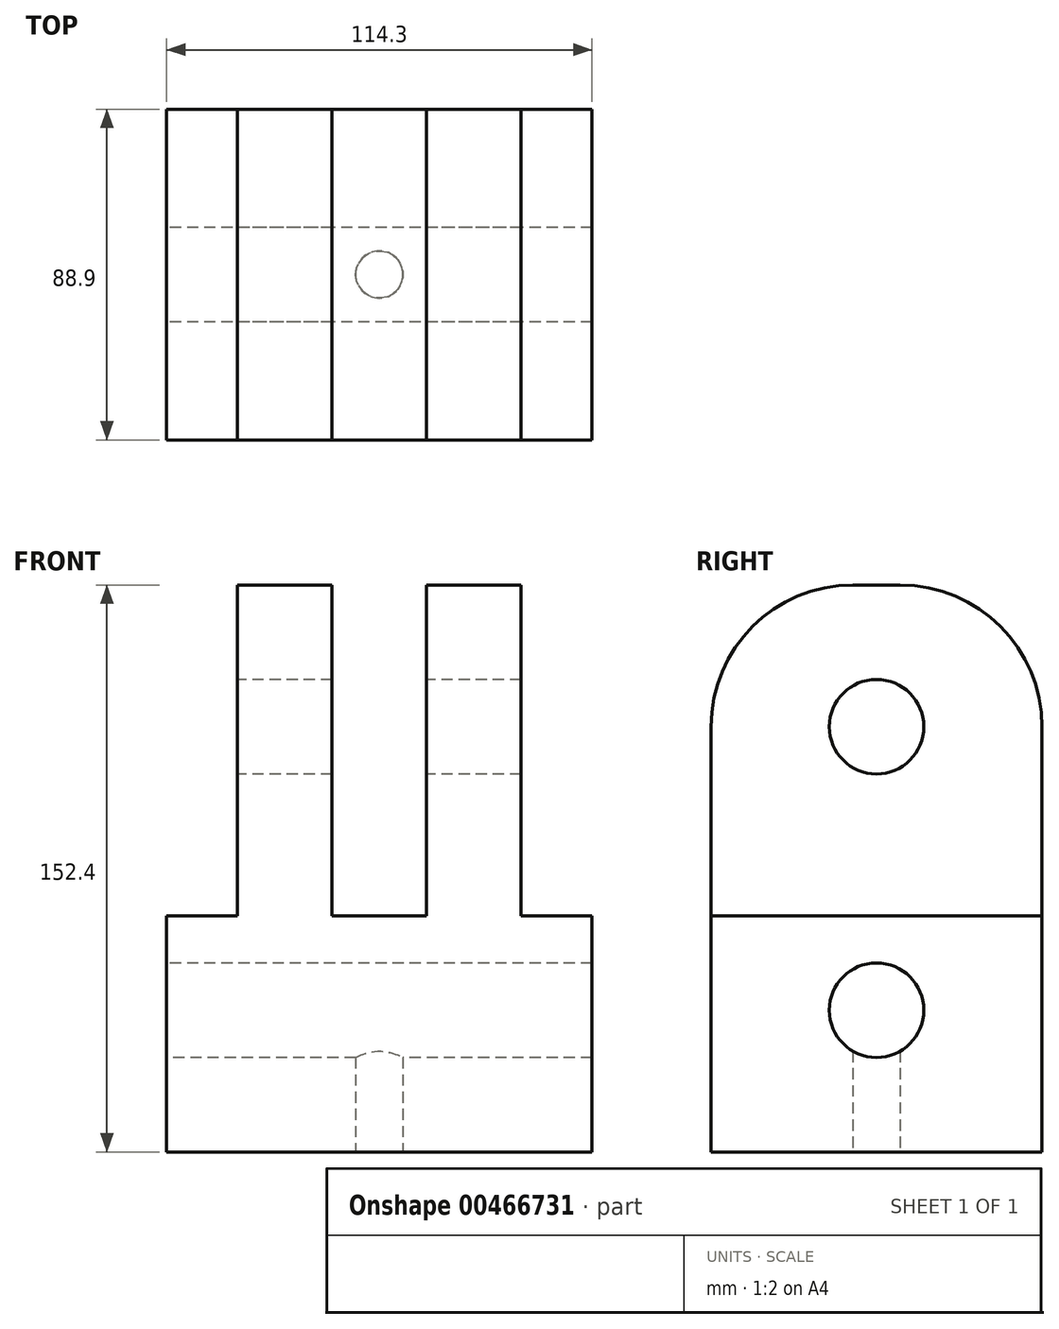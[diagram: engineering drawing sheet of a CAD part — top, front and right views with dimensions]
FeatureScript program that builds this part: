
annotation { "Feature Type Name" : "Feature", "Feature Type Description" : "" }
export const myFeature = defineFeature(function(context is Context, id is Id, definition is map)
    precondition{}
    {
        {
            var Q0;
            Q0=qCreatedBy(makeId("Top.planeOp"),FACE);
            var sketch = newSketch(context, id + "F0", { "sketchPlane" : qUnion([Q0])});
            skLineSegment(sketch, "E0.bottom", {"start": v(57.15, -44.45) * mm, "end": v(-57.15, -44.45) * mm});
            skLineSegment(sketch, "E0.top", {"start": v(57.15, 44.45) * mm, "end": v(-57.15, 44.45) * mm});
            skLineSegment(sketch, "E0.left", {"start": v(57.15, -44.45) * mm, "end": v(57.15, 44.45) * mm});
            skLineSegment(sketch, "E0.right", {"start": v(-57.15, -44.45) * mm, "end": v(-57.15, 44.45) * mm});
            skPoint(sketch, "E0.middle", {"position": v(0, 0) * mm});
            skSolve(sketch);
        }
        {
            var Q0;
            Q0=qSketchRegion(id+"F0",true);
            extrude(context, id + "F1", {"entities" : qUnion([Q0]), "depth" : 152.4 * mm});
        }
        {
            var Q0;
            Q0=makeQuery(id+"F1.opExtrude","SWEPT_FACE",FACE,{"disambiguationData":[OSD([sQuery(id+"F0.wireOp",EDGE,"E0.bottom")])]});
            var sketch = newSketch(context, id + "F2", { "sketchPlane" : qUnion([Q0])});
            skLineSegment(sketch, "E1.top", {"start": v(38.1, 63.5) * mm, "end": v(12.7, 63.5) * mm});
            skLineSegment(sketch, "E1.left", {"start": v(38.1, 152.4) * mm, "end": v(38.1, 63.5) * mm});
            skLineSegment(sketch, "E2.bottom", {"start": v(-12.7, 152.4) * mm, "end": v(-38.1, 152.4) * mm});
            skLineSegment(sketch, "E2.top", {"start": v(-12.7, 63.5) * mm, "end": v(-38.1, 63.5) * mm});
            skLineSegment(sketch, "E2.left", {"start": v(-12.7, 152.4) * mm, "end": v(-12.7, 63.5) * mm});
            skLineSegment(sketch, "E2.right", {"start": v(-38.1, 152.4) * mm, "end": v(-38.1, 63.5) * mm});
            skLineSegment(sketch, "E3", {"start": v(12.7, 152.4) * mm, "end": v(12.7, 63.5) * mm});
            skLineSegment(sketch, "E4", {"start": v(12.7, 63.5) * mm, "end": v(-12.7, 63.5) * mm});
            skLineSegment(sketch, "E5", {"start": v(-38.1, 63.5) * mm, "end": v(-57.15, 63.5) * mm});
            skPoint(sketch, "E5.endSnap0", {"position": v(-57.15, 76.2) * mm});
            skLineSegment(sketch, "E6", {"start": v(-57.15, 63.5) * mm, "end": v(38.1, 63.5) * mm});
            skLineSegment(sketch, "E7", {"start": v(38.1, 63.5) * mm, "end": v(57.15, 63.5) * mm});
            skSolve(sketch);
        }
        {
            var Q0;
            {var subQ0=sQuery(id+"F0.wireOp",EDGE,"E0.bottom");var subQ1=sQuery(id+"F0.wireOp",EDGE,"E0.left");Q0=makeQuery(id+"F6yg6DHshiw01AB_1.boolean.opBoolean","SPLIT",EDGE,{"disambiguationData":[TD([makeQuery(id+"F1.opExtrude","SWEPT_FACE",FACE,{"disambiguationData":[OSD([subQ1])]})])],"derivedFrom":makeQuery(id+"F1.opExtrude","CAP_EDGE",EDGE,{"disambiguationData":[OSD([subQ0])],"isStart":false})});}
            var Q1;
            {var subQ0=sQuery(id+"F0.wireOp",EDGE,"E0.bottom");Q1=makeQuery(id+"F6yg6DHshiw01AB_1.boolean.opBoolean","SPLIT",EDGE,{"disambiguationData":[TD([makeQuery(id+"F6yg6DHshiw01AB_1.opExtrude","SWEPT_FACE",FACE,{"disambiguationData":[OSD([sQuery(id+"F2.wireOp",EDGE,"E2.left")])]})])],"derivedFrom":makeQuery(id+"F1.opExtrude","CAP_EDGE",EDGE,{"disambiguationData":[OSD([subQ0])],"isStart":false})});}
            var Q2;
            {var subQ0=sQuery(id+"F0.wireOp",EDGE,"E0.bottom");var subQ1=sQuery(id+"F0.wireOp",EDGE,"E0.right");Q2=makeQuery(id+"F6yg6DHshiw01AB_1.boolean.opBoolean","SPLIT",EDGE,{"disambiguationData":[TD([makeQuery(id+"F1.opExtrude","SWEPT_FACE",FACE,{"disambiguationData":[OSD([subQ1])]})])],"derivedFrom":makeQuery(id+"F1.opExtrude","CAP_EDGE",EDGE,{"disambiguationData":[OSD([subQ0])],"isStart":false})});}
            var Q3;
            {var subQ0=sQuery(id+"F0.wireOp",EDGE,"E0.right");var subQ1=sQuery(id+"F0.wireOp",EDGE,"E0.top");Q3=makeQuery(id+"F6yg6DHshiw01AB_1.boolean.opBoolean","SPLIT",EDGE,{"disambiguationData":[TD([makeQuery(id+"F1.opExtrude","SWEPT_FACE",FACE,{"disambiguationData":[OSD([subQ0])]})])],"derivedFrom":makeQuery(id+"F1.opExtrude","CAP_EDGE",EDGE,{"disambiguationData":[OSD([subQ1])],"isStart":false})});}
            var Q4;
            {var subQ0=sQuery(id+"F0.wireOp",EDGE,"E0.top");Q4=makeQuery(id+"F6yg6DHshiw01AB_1.boolean.opBoolean","SPLIT",EDGE,{"disambiguationData":[TD([makeQuery(id+"F6yg6DHshiw01AB_1.opExtrude","SWEPT_FACE",FACE,{"disambiguationData":[OSD([sQuery(id+"F2.wireOp",EDGE,"E2.left")])]})])],"derivedFrom":makeQuery(id+"F1.opExtrude","CAP_EDGE",EDGE,{"disambiguationData":[OSD([subQ0])],"isStart":false})});}
            var Q5;
            {var subQ0=sQuery(id+"F0.wireOp",EDGE,"E0.left");var subQ1=sQuery(id+"F0.wireOp",EDGE,"E0.top");Q5=makeQuery(id+"F6yg6DHshiw01AB_1.boolean.opBoolean","SPLIT",EDGE,{"disambiguationData":[TD([makeQuery(id+"F1.opExtrude","SWEPT_FACE",FACE,{"disambiguationData":[OSD([subQ0])]})])],"derivedFrom":makeQuery(id+"F1.opExtrude","CAP_EDGE",EDGE,{"disambiguationData":[OSD([subQ1])],"isStart":false})});}
            fillet(context, id + "F3", {"entities" : qUnion([Q0, Q1, Q2, Q3, Q4, Q5]), "radius" : 38.1 * mm, "tangentPropagation" : true, "allowEdgeOverflow" : false});
        }
        {
            var Q0;
            Q0=makeQuery(id+"F1.opExtrude","SWEPT_FACE",FACE,{"disambiguationData":[OSD([sQuery(id+"F0.wireOp",EDGE,"E0.right")])]});
            var sketch = newSketch(context, id + "F4", { "sketchPlane" : qUnion([Q0])});
            skCircle(sketch, "E8", {"center": v(0, 38.1) * mm, "radius": 12.7 * mm});
            skCircle(sketch, "E9", {"center": v(0, 114.3) * mm, "radius": 12.7 * mm});
            skSolve(sketch);
        }
        {
            var Q0;
            Q0=qSketchRegion(id+"F4",true);
            extrude(context, id + "F5", {"entities" : qUnion([Q0]), "operationType" : NewBodyOperationType.REMOVE, "endBound" : BoundingType.THROUGH_ALL, "oppositeDirection" : true, "depth" : 25.4 * mm});
        }
        {
            var Q0;
            Q0=makeQuery(id+"F1.opExtrude","CAP_FACE",FACE,{"disambiguationData":[OSD([sQuery(id+"F0.wireOp",EDGE,"E0.bottom"),sQuery(id+"F0.wireOp",EDGE,"E0.top"),sQuery(id+"F0.wireOp",EDGE,"E0.left"),sQuery(id+"F0.wireOp",EDGE,"E0.right")])],"isStart":true});
            var sketch = newSketch(context, id + "F6", { "sketchPlane" : qUnion([Q0])});
            skCircle(sketch, "E10", {"center": v(0, 0) * mm, "radius": 6.35 * mm});
            skSolve(sketch);
        }
        {
            var Q0;
            Q0=qSketchRegion(id+"F6",true);
            extrude(context, id + "F7", {"entities" : qUnion([Q0]), "operationType" : NewBodyOperationType.REMOVE, "oppositeDirection" : true, "depth" : 38.1 * mm});
        }
        {
            var Q0;
            {var subQ0=sQuery(id+"F2.wireOp",EDGE,"E2.right");Q0=makeQuery(id+"F2.imprint","IMPRINT",FACE,{"disambiguationData":[TD([[makeQuery(id+"F2.imprint","IMPRINT",EDGE,{"derivedFrom":subQ0}),-1.0]])]});}
            var Q1;
            {var subQ0=sQuery(id+"F2.wireOp",EDGE,"E2.left");Q1=makeQuery(id+"F2.imprint","IMPRINT",FACE,{"disambiguationData":[TD([[makeQuery(id+"F2.imprint","IMPRINT",EDGE,{"derivedFrom":subQ0}),1.0]])]});}
            var Q2;
            {var subQ0=sQuery(id+"F2.wireOp",EDGE,"E1.left");Q2=makeQuery(id+"F2.imprint","IMPRINT",FACE,{"disambiguationData":[TD([[makeQuery(id+"F2.imprint","IMPRINT",EDGE,{"derivedFrom":subQ0}),1.0]])]});}
            extrude(context, id + "F8", {"entities" : qUnion([Q0, Q1, Q2]), "operationType" : NewBodyOperationType.REMOVE, "endBound" : BoundingType.THROUGH_ALL, "oppositeDirection" : true, "depth" : 25.4 * mm});
        }
    });
